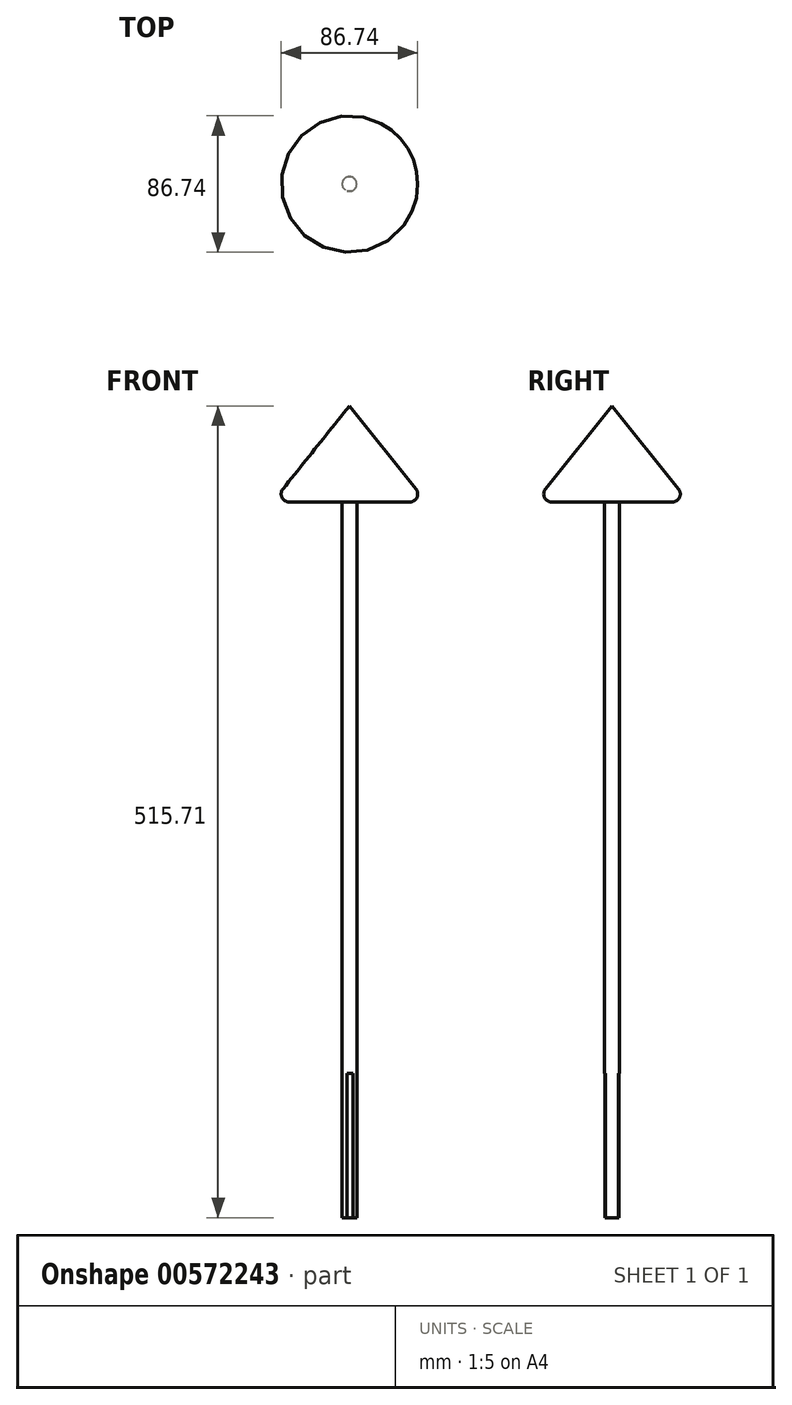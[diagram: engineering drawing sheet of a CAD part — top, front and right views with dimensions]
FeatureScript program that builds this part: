
annotation { "Feature Type Name" : "Feature", "Feature Type Description" : "" }
export const myFeature = defineFeature(function(context is Context, id is Id, definition is map)
    precondition{}
    {
        {
            var Q0;
            Q0=qCreatedBy(makeId("Right.planeOp"),FACE);
            var sketch = newSketch(context, id + "F0", { "sketchPlane" : qUnion([Q0])});
            skLineSegment(sketch, "E0", {"start": v(0, 0) * mm, "end": v(48.86, 0) * mm});
            skLineSegment(sketch, "E1", {"start": v(48.86, 0) * mm, "end": v(0, 61.05) * mm});
            skLineSegment(sketch, "E2", {"start": v(0, 61.05) * mm, "end": v(0, 1.92) * mm});
            skLineSegment(sketch, "E3", {"start": v(0, 1.92) * mm, "end": v(0, 0) * mm});
            skSolve(sketch);
        }
        {
            var Q0;
            Q0=makeQuery(id+"F0.imprint","IMPRINT",FACE,{"disambiguationData":[TD([[makeQuery(id+"F0.imprint","IMPRINT",EDGE,{"derivedFrom":sQuery(id+"F0.wireOp",EDGE,"E0")}),1.0]])]});
            var Q1;
            Q1=sQuery(id+"F0.wireOp",EDGE,"E2");
            revolve(context, id + "F1", {"entities" : qUnion([Q0]), "axis" : qUnion([Q1]), "revolveType" : RevolveType.FULL});
        }
        {
            var Q0;
            Q0=makeQuery(id+"F1.opRevolve","SWEPT_FACE",FACE,{"disambiguationData":[OSD([sQuery(id+"F0.wireOp",EDGE,"E1")])]});
            fillet(context, id + "F2", {"entities" : qUnion([Q0]), "radius" : 5.08 * mm, "tangentPropagation" : true, "allowEdgeOverflow" : false});
        }
        {
            var Q0;
            Q0=makeQuery(id+"F1.opRevolve","SWEPT_FACE",FACE,{"disambiguationData":[OSD([sQuery(id+"F0.wireOp",EDGE,"E0")])]});
            var sketch = newSketch(context, id + "F3", { "sketchPlane" : qUnion([Q0])});
            skCircle(sketch, "E4", {"center": v(0, 0) * mm, "radius": 4.64 * mm});
            skSolve(sketch);
        }
        {
            var Q0;
            Q0=makeQuery(id+"F3.imprint","IMPRINT",FACE,{"disambiguationData":[TD([[makeQuery(id+"F3.imprint","IMPRINT",EDGE,{"derivedFrom":sQuery(id+"F3.wireOp",EDGE,"E4")}),1.0]])]});
            extrude(context, id + "F4", {"entities" : qUnion([Q0]), "operationType" : NewBodyOperationType.ADD, "depth" : 454.66 * mm, "offsetDistance" : 25.4 * mm});
        }
        {
            var Q0;
            Q0=qCreatedBy(makeId("Front.planeOp"),FACE);
            var sketch = newSketch(context, id + "F5", { "sketchPlane" : qUnion([Q0])});
            skLineSegment(sketch, "E5", {"start": v(0, -454.71) * mm, "end": v(0, -363) * mm});
            skLineSegment(sketch, "E6", {"start": v(0, -363) * mm, "end": v(-1.48, -363) * mm});
            skLineSegment(sketch, "E7", {"start": v(-1.48, -363) * mm, "end": v(2.16, -363) * mm});
            skLineSegment(sketch, "E8", {"start": v(2.16, -363) * mm, "end": v(2.16, -454.86) * mm});
            skLineSegment(sketch, "E9", {"start": v(2.16, -454.86) * mm, "end": v(-1.48, -454.86) * mm});
            skLineSegment(sketch, "E10", {"start": v(-1.48, -454.86) * mm, "end": v(-1.48, -363) * mm});
            skSolve(sketch);
        }
        {
            var Q0;
            Q0 = qSketchRegion(id + "F5", true);
            extrude(context, id + "F6", {"entities" : qUnion([Q0]), "operationType" : NewBodyOperationType.ADD, "endBound" : BoundingType.SYMMETRIC, "depth" : 63.5 * mm, "offsetDistance" : 25.4 * mm});
        }
        {
            var Q0;
            {var subQ1=sQuery(id+"F3.wireOp",EDGE,"E4");var subQ2=sQuery(id+"F5.wireOp",EDGE,"E10");var subQ6=makeQuery(id+"F6.opExtrude","SWEPT_FACE",FACE,{"disambiguationData":[OSD([subQ2])]});Q0=makeQuery(id+"FW4FHYhvSr51Rrb_1.boolean.opBoolean","SPLIT",FACE,{"disambiguationData":[TD([makeQuery(id+"F4.opExtrude","CAP_FACE",FACE,{"disambiguationData":[OSD([subQ1])],"isStart":false})])],"derivedFrom":subQ6});}
            extrude(context, id + "F7", {"entities" : qUnion([Q0]), "operationType" : NewBodyOperationType.REMOVE, "endBound" : BoundingType.THROUGH_ALL, "oppositeDirection" : true, "depth" : 25.4 * mm, "offsetDistance" : 25.4 * mm});
        }
    });
